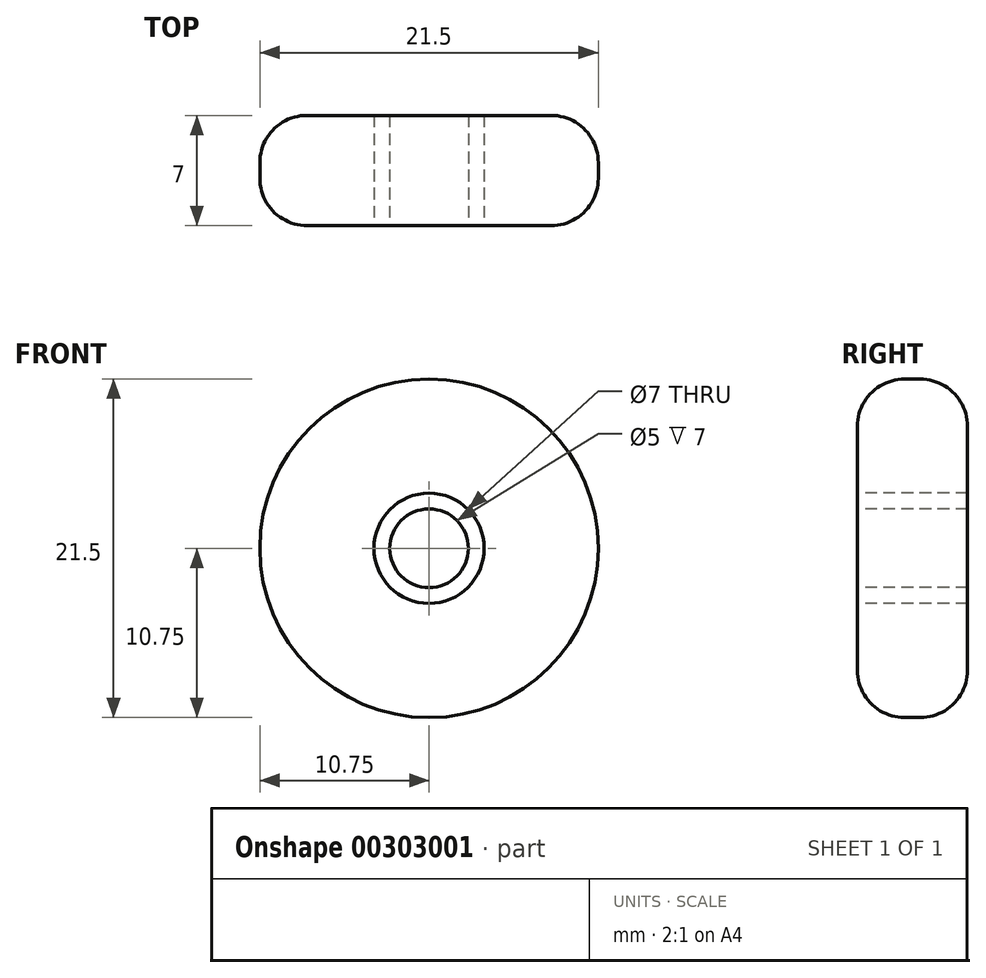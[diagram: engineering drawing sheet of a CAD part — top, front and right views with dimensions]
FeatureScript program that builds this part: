
annotation { "Feature Type Name" : "Feature", "Feature Type Description" : "" }
export const myFeature = defineFeature(function(context is Context, id is Id, definition is map)
    precondition{}
    {
        {
            var Q0;
            Q0=qCreatedBy(makeId("Front.planeOp"),FACE);
            var sketch = newSketch(context, id + "F0", { "sketchPlane" : qUnion([Q0])});
            skCircle(sketch, "E0", {"center": v(0, 0) * mm, "radius": 10.75 * mm});
            skCircle(sketch, "E1", {"center": v(0, 0) * mm, "radius": 7 * mm});
            skSolve(sketch);
        }
        {
            var Q0;
            Q0=makeQuery(id+"F0.imprint","IMPRINT",FACE,{"disambiguationData":[TD([[makeQuery(id+"F0.imprint","IMPRINT",EDGE,{"derivedFrom":sQuery(id+"F0.wireOp",EDGE,"E0")}),1.0]])]});
            extrude(context, id + "F1", {"entities" : qUnion([Q0]), "depth" : 7 * mm});
        }
        {
            var Q0;
            Q0=makeQuery(id+"F1.opExtrude","CAP_EDGE",EDGE,{"disambiguationData":[OSD([sQuery(id+"F0.wireOp",EDGE,"E0")])],"isStart":false});
            var Q1;
            Q1=makeQuery(id+"F1.opExtrude","CAP_EDGE",EDGE,{"disambiguationData":[OSD([sQuery(id+"F0.wireOp",EDGE,"E0")])],"isStart":true});
            fillet(context, id + "F2", {"entities" : qUnion([Q0, Q1]), "radius" : 3 * mm, "tangentPropagation" : true, "allowEdgeOverflow" : false});
        }
        {
            var Q0;
            Q0=makeQuery(id+"F1.opExtrude","CAP_FACE",FACE,{"disambiguationData":[OSD([sQuery(id+"F0.wireOp",EDGE,"E0"),sQuery(id+"F0.wireOp",EDGE,"E1")])],"isStart":false});
            var sketch = newSketch(context, id + "F3", { "sketchPlane" : qUnion([Q0])});
            skCircle(sketch, "E2", {"center": v(0, 0) * mm, "radius": 7 * mm});
            skCircle(sketch, "E3", {"center": v(0, 0) * mm, "radius": 3.5 * mm});
            skSolve(sketch);
        }
        {
            var Q0;
            Q0=makeQuery(id+"F3.imprint","IMPRINT",FACE,{"disambiguationData":[TD([[makeQuery(id+"F3.imprint","IMPRINT",EDGE,{"derivedFrom":sQuery(id+"F3.wireOp",EDGE,"E2")}),1.0]])]});
            extrude(context, id + "F4", {"entities" : qUnion([Q0]), "operationType" : NewBodyOperationType.ADD, "oppositeDirection" : true, "depth" : 7 * mm});
        }
        {
            var Q0;
            Q0=makeQuery(id+"F4.boolean.opBoolean","MERGE",FACE,{"derivedFrom":[makeQuery(id+"F1.opExtrude","CAP_FACE",FACE,{"disambiguationData":[OSD([sQuery(id+"F0.wireOp",EDGE,"E0"),sQuery(id+"F0.wireOp",EDGE,"E1")])],"isStart":false}),makeQuery(id+"F4.opExtrude","CAP_FACE",FACE,{"disambiguationData":[OSD([sQuery(id+"F3.wireOp",EDGE,"E2"),sQuery(id+"F3.wireOp",EDGE,"E3")])],"isStart":true})]});
            var sketch = newSketch(context, id + "F5", { "sketchPlane" : qUnion([Q0])});
            skCircle(sketch, "E4", {"center": v(0, 0) * mm, "radius": 3.5 * mm});
            skCircle(sketch, "E5", {"center": v(0, 0) * mm, "radius": 2.5 * mm});
            skSolve(sketch);
        }
        {
            var Q0;
            Q0=makeQuery(id+"F5.imprint","IMPRINT",FACE,{"disambiguationData":[TD([[makeQuery(id+"F5.imprint","IMPRINT",EDGE,{"derivedFrom":sQuery(id+"F5.wireOp",EDGE,"E4")}),1.0]])]});
            extrude(context, id + "F6", {"entities" : qUnion([Q0]), "oppositeDirection" : true, "depth" : 7 * mm});
        }
    });
